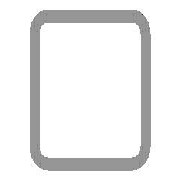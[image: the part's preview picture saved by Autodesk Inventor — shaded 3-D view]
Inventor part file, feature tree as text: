
AUTODESK INVENTOR PART (.ipt)
format: ipt  version: 2022 (Build 260153000, 153)  size: 144,384 bytes
history: native  units: mm (DEFAULTED — no unit token found)
features: other x4, sketch x3, plane x2, extrude x1, split x1
ambient origin geometry x8: Origin, YZ Plane, XZ Plane, XY Plane, X Axis, Y Axis, Z Axis, Center Point
bodies: Solid1 (feature_tree)
feature tree (11):
  parser-record x1  (decoder bookkeeping rows leaked as tree rows — omitted from the tree; the rows remain in map.json)
  other  "Driven Length"
  other  "Plano inicial"
  other  "Plano final"
  extrude  "Cuerpo"  TaperAngle=0.0deg  [1 undecoded]
  plane  "Plano de trabajo4"
  split  "Dividir1"
  sketch  "Boceto"  dims[d10=40.0mm d11=40.0mm d12=5.0mm d13=-0.0mm d14=450.0mm d15=20.0mm d16=20.0mm d17=90.0deg d18=450.0mm]
  sketch  "Sketch3"  dims[d3=450.0mm d4=0.0mm]
  plane  "Work Plane3"
  sketch  "Sketch4"  dims[d7=7.5mm]
note: 1 required parameter value undecoded (feature->parameter linkage not recoverable at this tier; creation-order binding heuristic only, values carry confidence <= 0.55)
